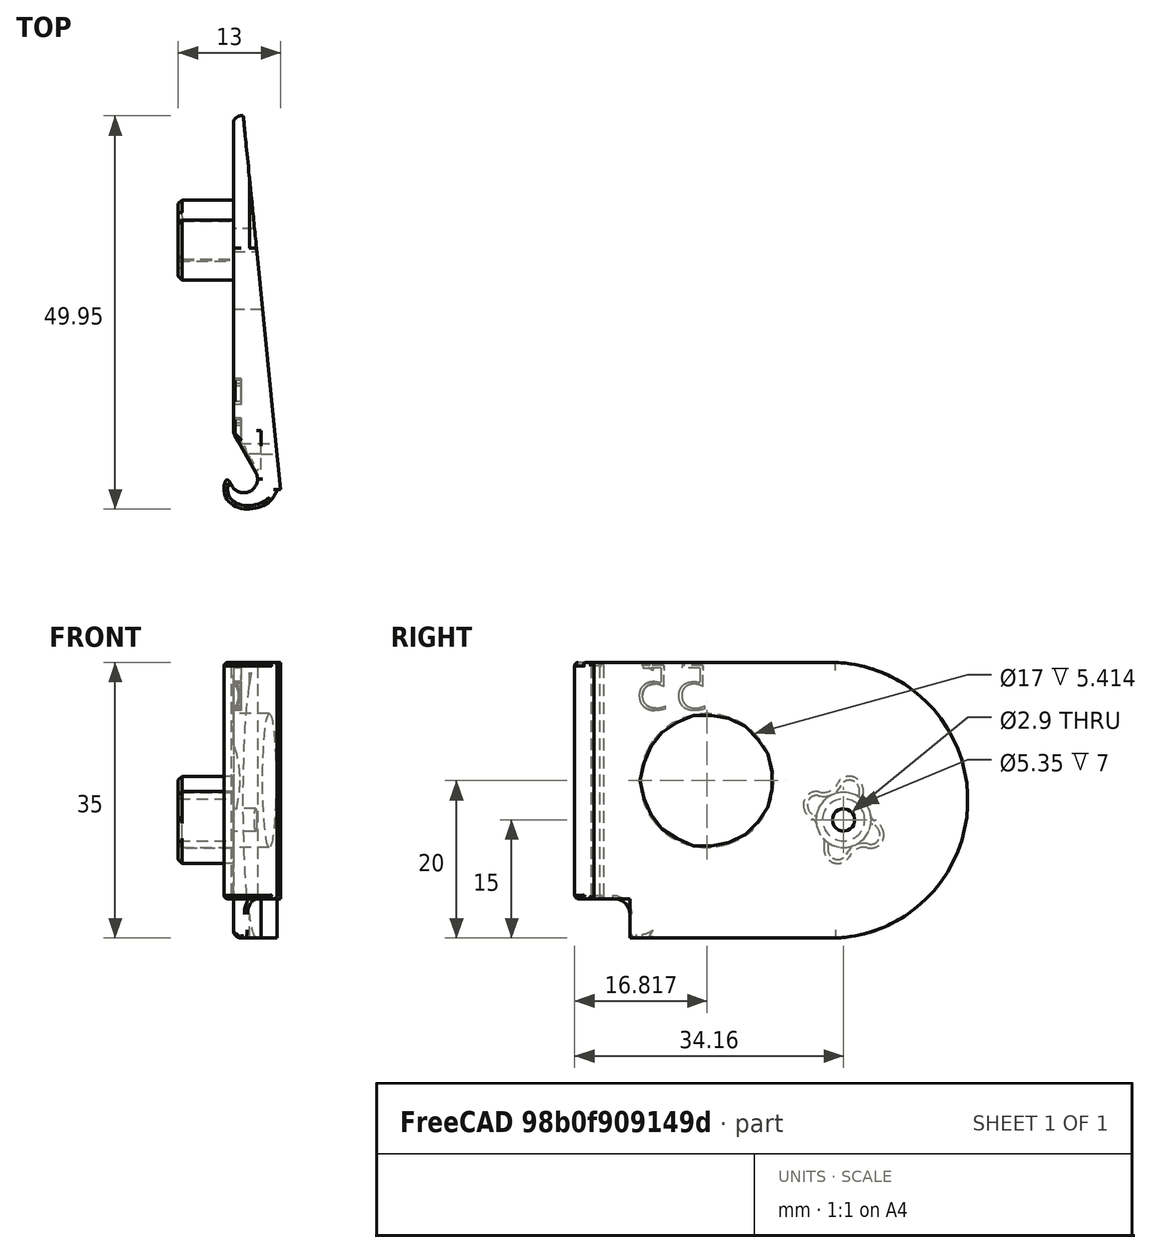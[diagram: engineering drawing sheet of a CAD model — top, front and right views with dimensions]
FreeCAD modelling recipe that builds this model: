
FCSTD DOCUMENT  (FreeCAD 0.18R)
Label: hinge-left-155deg-angled
License: All rights reserved
LicenseURL: http://en.wikipedia.org/wiki/All_rights_reserved
objects: App::FeaturePython×4, Part::FeaturePython×2, Part::Part2DObjectPython×1, Part::Extrusion×1, Part::Cut×1
note: 5 computed .brp shape members not serialized (recipe doc carries the construction recipe); baked Part::Feature solids carry a one-line shape summary decoded from their .brp

FEATURE [Part::FeaturePython] bracket_left_001  label="bracket-left_001"  # a2plus imported part (geometry in sourceFile) (typed FeaturePython)
  a2p_Version = V0.1
  fixedPosition = true
  objectType = a2pPart
  sourceFile = ./parts/bracket-left.fcstd
  subassemblyImport = false
  timeLastImport = 1.60454e+09
  updateColors = true
FEATURE [Part::FeaturePython] pillar_base_001  label="pillar-base_001"  # a2plus imported part (geometry in sourceFile) (typed FeaturePython)
  Placement = pos=(0.000608724,-0.00262051,0.00478212) rot=(1,0,0;6.28301rad)
  a2p_Version = V0.1
  fixedPosition = false
  objectType = a2pPart
  sourceFile = ./parts/pillar-base.fcstd
  subassemblyImport = false
  timeLastImport = 1.60452e+09
  updateColors = true
FEATURE [Part::Part2DObjectPython] ShapeString  # Draft 2D object (typed FeaturePython)
  FontFile = <path>
  Placement = pos=(1.61,10.5,29) rot=(0.57735,-0.57735,-0.57735;2.0944rad)
  Size = 6
  String = 55
  Tracking = 0
FEATURE [Part::Extrusion] Extrude
  Base = -> ShapeString
  Dir = (-1,-1e-16,2e-16)
  DirMode = 2
  FaceMakerClass = Part::FaceMakerBullseye
  LengthFwd = 2
  LengthRev = 0
  Solid = false
  Symmetric = false
FEATURE [App::FeaturePython] axisCoincident_001  label="axisCoincident_001__bracket-left_001"  # a2plus constraint (typed FeaturePython)
  Object1 = pillar_base_001
  Object2 = bracket_left_001
  ParentTreeObject = -> pillar_base_001
  SubElement1 = Face17
  SubElement2 = Face39
  Suppressed = false
  Type = axial
  directionConstraint = 1
  lockRotation = false
FEATURE [App::FeaturePython] axisCoincident_001_mirror  label="axisCoincident_001__pillar-base_001"  # a2plus constraint (typed FeaturePython)
  Object1 = pillar_base_001
  Object2 = bracket_left_001
  ParentTreeObject = -> bracket_left_001
  SubElement1 = Face17
  SubElement2 = Face39
  Suppressed = false
  Type = axial
  directionConstraint = 1
  lockRotation = false
FEATURE [App::FeaturePython] planeCoincident_001  label="planeCoincident_001__bracket-left_001"  # a2plus constraint (typed FeaturePython)
  Object1 = pillar_base_001
  Object2 = bracket_left_001
  ParentTreeObject = -> pillar_base_001
  SubElement1 = Face1
  SubElement2 = Face65
  Suppressed = false
  Type = plane
  directionConstraint = 0
  offset = 0
FEATURE [App::FeaturePython] planeCoincident_001_mirror  label="planeCoincident_001__pillar-base_001"  # a2plus constraint (typed FeaturePython)
  Object1 = pillar_base_001
  Object2 = bracket_left_001
  ParentTreeObject = -> bracket_left_001
  SubElement1 = Face1
  SubElement2 = Face65
  Suppressed = false
  Type = plane
  directionConstraint = 0
  offset = 0
FEATURE [Part::Cut] Cut
  Base = -> bracket_left_001
  Tool = -> Extrude
note: 1 file-system path scrubbed to <path> (originals preserved in the JSON sidecar)
